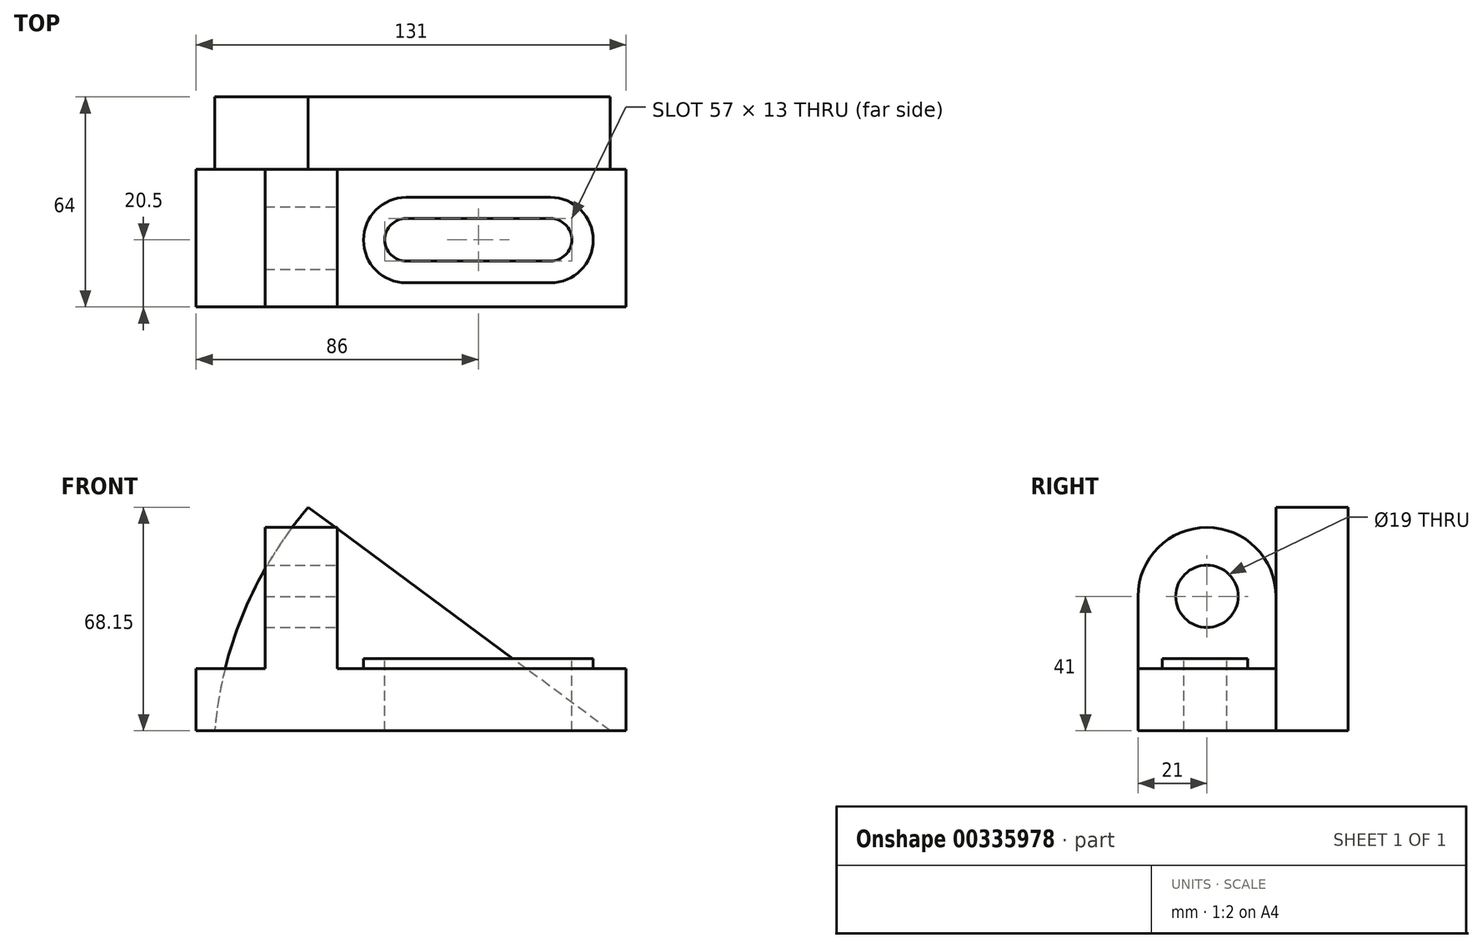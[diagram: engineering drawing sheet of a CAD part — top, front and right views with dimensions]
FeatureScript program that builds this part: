
annotation { "Feature Type Name" : "Feature", "Feature Type Description" : "" }
export const myFeature = defineFeature(function(context is Context, id is Id, definition is map)
    precondition{}
    {
        {
            var Q0;
            Q0=qCreatedBy(makeId("Front.planeOp"),FACE);
            var sketch = newSketch(context, id + "F0", { "sketchPlane" : qUnion([Q0])});
            skLineSegment(sketch, "E0.bottom", {"start": v(0, 0) * mm, "end": v(131, 0) * mm});
            skLineSegment(sketch, "E0.top", {"start": v(0, 19) * mm, "end": v(131, 19) * mm});
            skLineSegment(sketch, "E0.left", {"start": v(0, 0) * mm, "end": v(0, 19) * mm});
            skLineSegment(sketch, "E0.right", {"start": v(131, 0) * mm, "end": v(131, 19) * mm});
            skSolve(sketch);
        }
        {
            var Q0;
            Q0 = qSketchRegion(id + "F0", true);
            extrude(context, id + "F1", {"entities" : qUnion([Q0]), "oppositeDirection" : true, "depth" : 42 * mm});
        }
        {
            var Q0;
            Q0=makeQuery(id+"F1.opExtrude","CAP_FACE",FACE,{"disambiguationData":[OSD([sQuery(id+"F0.wireOp",EDGE,"E0.bottom"),sQuery(id+"F0.wireOp",EDGE,"E0.top"),sQuery(id+"F0.wireOp",EDGE,"E0.left"),sQuery(id+"F0.wireOp",EDGE,"E0.right")])],"isStart":true});
            var sketch = newSketch(context, id + "F2", { "sketchPlane" : qUnion([Q0])});
            skLineSegment(sketch, "E1.bottom", {"start": v(21, 19) * mm, "end": v(43, 19) * mm});
            skLineSegment(sketch, "E1.top", {"start": v(21, 41) * mm, "end": v(43, 41) * mm});
            skLineSegment(sketch, "E1.left", {"start": v(21, 19) * mm, "end": v(21, 41) * mm});
            skLineSegment(sketch, "E1.right", {"start": v(43, 19) * mm, "end": v(43, 41) * mm});
            skSolve(sketch);
        }
        {
            var Q0;
            Q0 = qSketchRegion(id + "F2", true);
            extrude(context, id + "F3", {"entities" : qUnion([Q0]), "operationType" : NewBodyOperationType.ADD, "oppositeDirection" : true, "depth" : 42 * mm});
        }
        {
            var Q0;
            Q0=makeQuery(id+"F3.opExtrude","SWEPT_FACE",FACE,{"disambiguationData":[OSD([sQuery(id+"F2.wireOp",EDGE,"E1.right")])]});
            var sketch = newSketch(context, id + "F4", { "sketchPlane" : qUnion([Q0])});
            skArc(sketch, "E2", {"start": v(42, 41) * mm, "mid": v(21, 62) * mm, "end": v(0, 41) * mm});
            skLineSegment(sketch, "E3", {"start": v(42, 41) * mm, "end": v(0, 41) * mm});
            skSolve(sketch);
        }
        {
            var Q0;
            Q0 = qSketchRegion(id + "F4", true);
            extrude(context, id + "F5", {"entities" : qUnion([Q0]), "operationType" : NewBodyOperationType.ADD, "oppositeDirection" : true, "depth" : 22 * mm});
        }
        {
            var Q0;
            Q0=makeQuery(id+"F5.boolean.opBoolean","MERGE",FACE,{"derivedFrom":[makeQuery(id+"F3.opExtrude","SWEPT_FACE",FACE,{"disambiguationData":[OSD([sQuery(id+"F2.wireOp",EDGE,"E1.right")])]}),makeQuery(id+"F5.opExtrude","CAP_FACE",FACE,{"disambiguationData":[OSD([sQuery(id+"F4.wireOp",EDGE,"E2"),sQuery(id+"F4.wireOp",EDGE,"E3")])],"isStart":true})]});
            var sketch = newSketch(context, id + "F6", { "sketchPlane" : qUnion([Q0])});
            skCircle(sketch, "E4", {"center": v(21, 41) * mm, "radius": 9.5 * mm});
            skSolve(sketch);
        }
        {
            var Q0;
            Q0 = qSketchRegion(id + "F6", true);
            extrude(context, id + "F7", {"entities" : qUnion([Q0]), "operationType" : NewBodyOperationType.REMOVE, "endBound" : BoundingType.THROUGH_ALL, "oppositeDirection" : true, "depth" : 25 * mm});
        }
        {
            var Q0;
            {var subQ4=sQuery(id+"F0.wireOp",EDGE,"E0.right");var subQ6=sQuery(id+"F0.wireOp",EDGE,"E0.top");Q0=makeQuery(id+"F3.boolean.opBoolean","SPLIT",FACE,{"disambiguationData":[TD([makeQuery(id+"F1.opExtrude","SWEPT_FACE",FACE,{"disambiguationData":[OSD([subQ4])]})])],"derivedFrom":makeQuery(id+"F1.opExtrude","SWEPT_FACE",FACE,{"disambiguationData":[OSD([subQ6])]})});}
            var sketch = newSketch(context, id + "F8", { "sketchPlane" : qUnion([Q0])});
            skLineSegment(sketch, "E5.bottom", {"start": v(64, 14) * mm, "end": v(108, 14) * mm});
            skLineSegment(sketch, "E5.top", {"start": v(64, 27) * mm, "end": v(108, 27) * mm});
            skArc(sketch, "E6", {"start": v(108, 14) * mm, "mid": v(114.5, 20.5) * mm, "end": v(108, 27) * mm});
            skArc(sketch, "E7", {"start": v(64, 27) * mm, "mid": v(57.5, 20.5) * mm, "end": v(64, 14) * mm});
            skSolve(sketch);
        }
        {
            var Q0;
            Q0 = qSketchRegion(id + "F8", true);
            extrude(context, id + "F9", {"entities" : qUnion([Q0]), "operationType" : NewBodyOperationType.REMOVE, "endBound" : BoundingType.THROUGH_ALL, "oppositeDirection" : true, "depth" : 25 * mm});
        }
        {
            var Q0;
            {var subQ4=sQuery(id+"F0.wireOp",EDGE,"E0.right");var subQ6=sQuery(id+"F0.wireOp",EDGE,"E0.top");Q0=makeQuery(id+"F3.boolean.opBoolean","SPLIT",FACE,{"disambiguationData":[TD([makeQuery(id+"F1.opExtrude","SWEPT_FACE",FACE,{"disambiguationData":[OSD([subQ4])]})])],"derivedFrom":makeQuery(id+"F1.opExtrude","SWEPT_FACE",FACE,{"disambiguationData":[OSD([subQ6])]})});}
            var sketch = newSketch(context, id + "F10", { "sketchPlane" : qUnion([Q0])});
            skLineSegment(sketch, "E8", {"start": v(64, 33.4) * mm, "end": v(108, 33.4) * mm});
            skLineSegment(sketch, "E9", {"start": v(64, 7.4) * mm, "end": v(108, 7.4) * mm});
            skArc(sketch, "E10", {"start": v(108, 7.4) * mm, "mid": v(121, 20.4) * mm, "end": v(108, 33.4) * mm});
            skArc(sketch, "E11", {"start": v(64, 33.4) * mm, "mid": v(51, 20.4) * mm, "end": v(64, 7.4) * mm});
            skSolve(sketch);
        }
        {
            var Q0;
            Q0=makeQuery(id+"F3.boolean.opBoolean","MERGE",FACE,{"derivedFrom":[makeQuery(id+"F1.opExtrude","CAP_FACE",FACE,{"disambiguationData":[OSD([sQuery(id+"F0.wireOp",EDGE,"E0.bottom"),sQuery(id+"F0.wireOp",EDGE,"E0.top"),sQuery(id+"F0.wireOp",EDGE,"E0.left"),sQuery(id+"F0.wireOp",EDGE,"E0.right")])],"isStart":false}),makeQuery(id+"F3.opExtrude","CAP_FACE",FACE,{"disambiguationData":[OSD([sQuery(id+"F2.wireOp",EDGE,"E1.bottom"),sQuery(id+"F2.wireOp",EDGE,"E1.top"),sQuery(id+"F2.wireOp",EDGE,"E1.left"),sQuery(id+"F2.wireOp",EDGE,"E1.right")])],"isStart":false})]});
            var sketch = newSketch(context, id + "F11", { "sketchPlane" : qUnion([Q0])});
            skLineSegment(sketch, "E12", {"start": v(-126.2, 0) * mm, "end": v(-34.16, 68.15) * mm});
            skLineSegment(sketch, "E13", {"start": v(-126.2, 0) * mm, "end": v(-5.64, 0) * mm});
            skArc(sketch, "E14", {"start": v(-5.64, 0) * mm, "mid": v(-14.57, 36.3) * mm, "end": v(-34.16, 68.15) * mm});
            skSolve(sketch);
        }
        {
            var Q0;
            Q0 = qSketchRegion(id + "F11", true);
            extrude(context, id + "F12", {"entities" : qUnion([Q0]), "operationType" : NewBodyOperationType.ADD, "depth" : 22 * mm});
        }
        {
            var Q0;
            Q0=makeQuery(id+"F10.imprint","IMPRINT",FACE,{"disambiguationData":[TD([[makeQuery(id+"F10.imprint","IMPRINT",EDGE,{"derivedFrom":sQuery(id+"F10.wireOp",EDGE,"E8")}),-1.0]])]});
            extrude(context, id + "F13", {"entities" : qUnion([Q0]), "operationType" : NewBodyOperationType.ADD, "depth" : 3 * mm});
        }
    });
